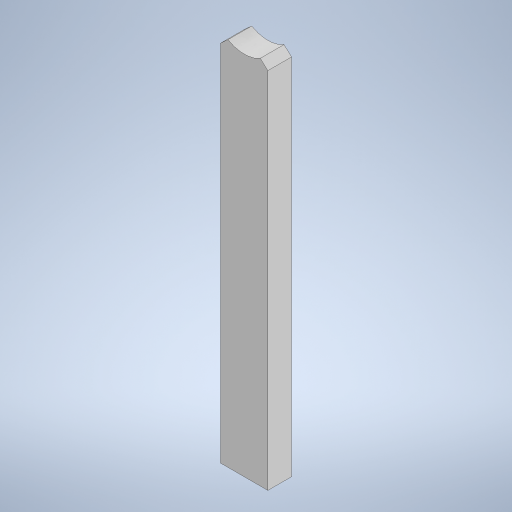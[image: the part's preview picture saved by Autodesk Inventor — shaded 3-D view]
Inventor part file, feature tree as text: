
AUTODESK INVENTOR PART (.ipt)
format: ipt  version: 2023 (Build 270158000, 158)  size: 232,960 bytes
history: native  units: mm
features: extrude x1, sketch x1
ambient origin geometry x8: Origin, YZ Plane, XZ Plane, XY Plane, X Axis, Y Axis, Z Axis, Center Point
bodies: Solid1 (feature_tree)
feature tree (2):
  extrude  "Extrusion1"  Depth=15.0mm
  sketch  "Sketch2"  dims[d3=24.03232mm d4=16.648713mm d5=4.353348mm d15=230.0mm d16=230.0mm d17=15.0mm d18=0.0mm]
